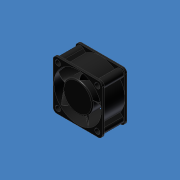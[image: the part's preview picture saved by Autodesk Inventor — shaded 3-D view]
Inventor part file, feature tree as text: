
AUTODESK INVENTOR PART (.ipt)
format: ipt  version: 2014 SP1 (Build 180222100, 222)  size: 395,776 bytes
history: native  units: mm (DEFAULTED — no unit token found)
features: sketch x10, extrude x6, hole x2, pattern_circular x2, fillet x2, revolve x1, plane x1, helix x1
ambient origin geometry x8: Origin, YZ Plane, XZ Plane, XY Plane, X Axis, Y Axis, Z Axis, Center Point
bodies: Solid1 (feature_tree)
feature tree (25):
  extrude  "Extrusion1"  Depth=20.066mm TaperAngle=0.0deg
  revolve  "Revolution1"  [1 undecoded]
  hole  "Hole3"  [1 undecoded]
  extrude  "Extrusion3"  Depth=32.004mm
  pattern_circular  "Circular Pattern2"  Count=4 Angle=360.0deg
  fillet  "Fillet2"  Radius=3.175mm
  hole  "Hole4"  [1 undecoded]
  extrude  "Extrusion4"  Depth=12.446mm
  extrude  "Extrusion5"  Depth=12.065mm
  extrude  "Extrusion6"  Depth=1.4732mm
  extrude  "Extrusion7"  TaperAngle=135.0deg  [1 undecoded]
  fillet  "Fillet3"  Radius=12.065mm
  plane  "Work Plane1"
  helix  "Coil2"  [1 undecoded]
  pattern_circular  "Circular Pattern4"  [2 undecoded]
  sketch  "Sketch1"  dims[d0=39.878mm d1=20.066mm d2=0.0mm]
  sketch  "Sketch2"  dims[d3=1.7018mm d4=12.7mm]
  sketch  "Sketch6"  dims[d5=1.7018mm d6=90.0deg]
  sketch  "Sketch7"  dims[d28=32.004mm d29=32.004mm]
  sketch  "Sketch8"  dims[d30=4.318mm d31=12.7mm d32=9.525mm d33=6.35mm d34=14.3117mm d35=19.05mm d36=20.594885mm]
  sketch  "Sketch9"  dims[d37=6.35mm]
  sketch  "Sketch10"  dims[d38=19.812mm d39=0.0mm d40=40.0mm d42=360.0deg d43=3.175mm]
  sketch  "Sketch11"  dims[d44=38.481mm d45=12.7mm d46=9.525mm d47=6.35mm d48=14.3117mm d49=19.05mm d50=20.594885mm d51=24.13mm]
  sketch  "Sketch12"  dims[d52=1.4732mm d53=1.4732mm d54=12.446mm]
  sketch  "Sketch13"  dims[d55=5.9944mm d57=12.065mm d58=12.065mm d59=1.4732mm d60=135.0deg d61=12.065mm d62=12.065mm d63=3.81mm d64=0.0mm d65=1.016mm d66=1.016mm d67=1.016mm d68=1.016mm d69=2.032mm d70=0.0mm d71=1.0922mm d72=2.54mm d73=0.0mm d74=23.876mm d75=16.256mm d76=0.0mm d77=0.7874mm d83=0.698132mm d84=2.094395mm d85=37.338mm d86=0.254mm d98=-0.762mm d99=25.4mm d100=13.97mm d101=1.5mm d102=0.0mm d103=90.0deg d104=90.0deg d105=0.0mm d106=0.0mm d107=50.0mm d109=360.0deg]
note: 7 required parameter values undecoded (feature->parameter linkage not recoverable at this tier; creation-order binding heuristic only, values carry confidence <= 0.55)